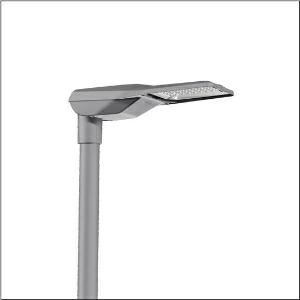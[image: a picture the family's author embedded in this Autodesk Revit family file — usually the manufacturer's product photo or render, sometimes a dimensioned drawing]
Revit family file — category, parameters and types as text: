
# Revit family: streetlight_sl_21_mini___st1_0a_5xe6d43a08hb_530a
name_source: partatom
category: Lighting Fixtures
units: mm (PartAtom-declared; Revit-internal decimal feet)

## family parameters
Cut with Voids When Loaded = No
Host = Face
Light Source = No
Part Type = Normal
Room Calculation Point = No
Round Connector Dimension = Use Diameter
Shared = No

## types (1)
- --- (1 x LED, 9430 lm, 66 W, 4000K)
    Apparent Load = 66 VA
    CIE Flux Codes = 37 72 97 100 100
    Color Rendering = 70
    Color Temperature = 4000K
    Default Elevation = 1800 mm
    Description = Streetlight SL 21 mini, mast luminaire, primary light control with lens, of PMMA, primary optical cover: cover, of toughened safety glass, transparent, light distribution: ST1.0a, light emission: direct distribution, primary light characteristic: asymmetric, installation type: post-top, side-entry, LED, 3G 1.5mm², High Power LED, rated luminous flux: 9.430lm, luminous efficacy: 143lm/W, light colour: 740, colour temperature: 4000K, control: overheat protection, constant luminous flux control, time-dependent luminous flux control, flexible luminous flux parameterisation, mains connection: 230..240V, AC, 50/60Hz, connection cable pre-assembled, cable length: 8,5m, wiring characteristics: H07RN-F, start of lifetime: 66W, end of service life: 69W, reduction: 30W, luminaire housing, of diecast aluminium, powder-coated, Siteco® metallic grey (DB 702S), corrosivity category C5 mid according to DIN EN ISO 12944, please order mast flange separately, inclination adjustable: 0°, 5°, 10°, 15°, sealing non-destructively replaceable, multi-level sealing system, length: 628mm, width: 235mm, height: 110mm, mast flange for spigot size: 42mm (side-entry): 5XC10008XM4, 60/48mm (side-entry/post-top): 5XC10108XM2, 76/60mm (side-entry/post-top): 5XC10108XM1, protection rating (complete): IP66, insulation class (complete): insulation class II (safety insulation), certification: CE, ENEC, ENEC+, VDE, impact resistance: IK09, permissible operating ambient temperature for outdoor applications: -40..+50°C, standard-compliant lighting for roads and squares, packaging unit: 1 piece

Light Distribution: ST1.0a
    Height = 110 mm
    Lamp = 1 x LED
    Lamp Light Flux = 9430 lm
    Lamp Power = 66 W
    Lamp count = 1
    Length = 625 mm
    Luminous efficacy = 143 lm/W
    Manufacturer = Siteco
    ModVariant = No
    Model = 5XE6D43A08HB
    Number of Poles = 1
    OnlyDefault = Yes
    Power Factor = 1
    Product Name = Streetlight SL 21 mini | ST1.0a
    Product group = mast luminaire | pylon top
    ProductGroupID = 6100
    Protection Class = Protection class II
    Protection Degree = IP 66
    RLX_Detail_Level = 1
    RLX_Emergency_Light_Flux = 0 lm
    RLX_Emergency_Type = 0
    RLX_Emergency_Type_DB = No
    RlxData = <blob elided: 93401 chars, md5=78e05141>
    Socket = socket
    Standby Power = 0 W
    System Light Flux = 9430 lm
    System Power = 66 W
    Type Comments = factory setting: luminous flux: 100 % | Output Level: 100 % | 670 mA
    Type Image = l_1003519.jpg
    URL = http://relux.com
    VarID = @adj_121939
    Voltage = 0 V
    Weight = 0.00 kg
    Width = 234 mm

## geometry (parser evidence)
native form markers: Blend x4, Sweep x10
no freeform markers — native parametric forms only
